# Revit family: Скамейка стальная «Квадрант» без спинки Арт 12410
name_source: partatom
category: Антураж
revit_build: Autodesk Revit 2018 (Build: 20180423_1000(x64)
units: mm (PartAtom-declared; Revit-internal decimal feet)

## family parameters
Всегда вертикально = Да
Источник визуального образа = Геометрия семейства
На основе рабочей плоскости = Нет
Общий = Нет
При загрузке вырезать с полостями = Нет
Точка расчета площади = Нет

## types (2) — shared parameters
L1 = 1050 мм
L2 = 2100 мм
URL = https://hobbyka.ru
W1 = 1050 мм
W2 = 2100 мм
Артикул товара = Арт. 12410
Высота = 650 мм
Группа модели = Садовые скамейки
Изготовитель = ООО «Хоббика»
Материал изделия = Сталь, дерево

## per-type parameters (varying)
| type | 1 Элемент | Длина | Изображение типоразмера | Круглая | Описание | Ширина |
| Стандарт | Да | 1050 мм | Скамейка стальная «Квадрант» без спинки стандарт Арт 12410.jpg | Нет | Скамейка стальная «Квадрант» без спинки. Версия стандарт | 1050 мм |
| Круглая | Нет | 2100 мм | Скамейка стальная «Квадрант» без спинки круглая Арт 12410.jpg | Да | Скамейка стальная «Квадрант» без спинки. Версия круглая | 2100 мм |
